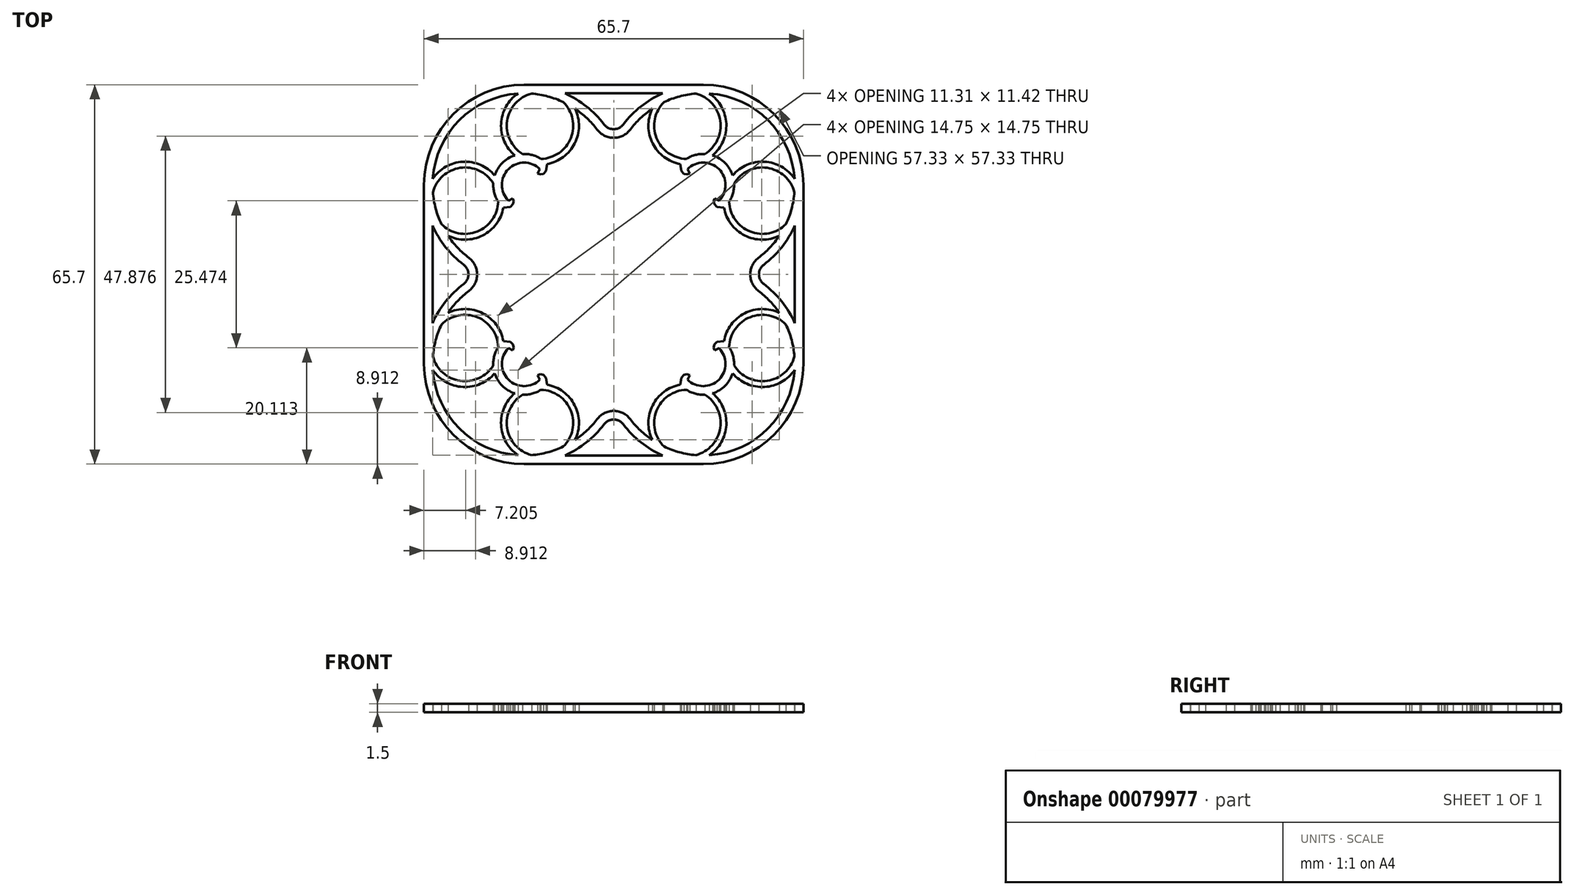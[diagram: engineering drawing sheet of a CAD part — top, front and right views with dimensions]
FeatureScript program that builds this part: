
annotation { "Feature Type Name" : "Feature", "Feature Type Description" : "" }
export const myFeature = defineFeature(function(context is Context, id is Id, definition is map)
    precondition{}
    {
        {
            var Q0;
            Q0=qCreatedBy(makeId("Top.planeOp"),FACE);
            var sketch = newSketch(context, id + "F0", { "sketchPlane" : qUnion([Q0])});
            skLineSegment(sketch, "E0.bottom", {"start": v(-15.5, 15.5) * mm, "end": v(15.5, 15.5) * mm});
            skLineSegment(sketch, "E0.top", {"start": v(-15.5, -15.5) * mm, "end": v(15.5, -15.5) * mm});
            skLineSegment(sketch, "E0.left", {"start": v(-15.5, 15.5) * mm, "end": v(-15.5, -15.5) * mm});
            skLineSegment(sketch, "E0.right", {"start": v(15.5, 15.5) * mm, "end": v(15.5, -15.5) * mm});
            skPoint(sketch, "E0.middle", {"position": v(0, 0) * mm});
            skCircle(sketch, "E1", {"center": v(-15.5, 15.5) * mm, "radius": 15 * mm});
            skCircle(sketch, "E2", {"center": v(15.5, 15.5) * mm, "radius": 15 * mm});
            skCircle(sketch, "E3", {"center": v(-15.5, -15.5) * mm, "radius": 15 * mm});
            skCircle(sketch, "E4", {"center": v(15.5, -15.5) * mm, "radius": 15 * mm});
            skLineSegment(sketch, "E5.bottom", {"start": v(-10, 10) * mm, "end": v(10, 10) * mm});
            skLineSegment(sketch, "E5.top", {"start": v(-10, -10) * mm, "end": v(10, -10) * mm});
            skLineSegment(sketch, "E5.left", {"start": v(-10, 10) * mm, "end": v(-10, -10) * mm});
            skLineSegment(sketch, "E5.right", {"start": v(10, 10) * mm, "end": v(10, -10) * mm});
            skCircle(sketch, "E6", {"center": v(-15.5, 15.5) * mm, "radius": 4.5 * mm});
            skCircle(sketch, "E7", {"center": v(-15.5, 15.5) * mm, "radius": 3.5 * mm});
            skCircle(sketch, "E8", {"center": v(15.5, 15.5) * mm, "radius": 3.5 * mm});
            skCircle(sketch, "E9", {"center": v(15.5, 15.5) * mm, "radius": 4.5 * mm});
            skCircle(sketch, "E10", {"center": v(15.5, -15.5) * mm, "radius": 4.5 * mm});
            skCircle(sketch, "E11", {"center": v(15.5, -15.5) * mm, "radius": 3.5 * mm});
            skCircle(sketch, "E12", {"center": v(-15.5, -15.5) * mm, "radius": 3.5 * mm});
            skCircle(sketch, "E13", {"center": v(-15.5, -15.5) * mm, "radius": 4.5 * mm});
            skLineSegment(sketch, "E14", {"start": v(-15.5, 15.5) * mm, "end": v(-18.68, 12.32) * mm});
            skLineSegment(sketch, "E15", {"start": v(-18.68, 12.32) * mm, "end": v(-12.32, 18.68) * mm});
            skLineSegment(sketch, "E16", {"start": v(-17.9, 11.7) * mm, "end": v(-11.7, 17.9) * mm});
            skLineSegment(sketch, "E17", {"start": v(-13.24, 16.34) * mm, "end": v(-13.95, 17.05) * mm});
            skSolve(sketch);
        }
        {
            var Q0;
            Q0=qCreatedBy(makeId("Top.planeOp"),FACE);
            var sketch = newSketch(context, id + "F1", { "sketchPlane" : qUnion([Q0])});
            skPoint(sketch, "E18.0", {"position": v(-15.5, 15.5) * mm});
            skArc(sketch, "E19", {"start": v(-12.6, 20) * mm, "mid": v(-14.12, 20.67) * mm, "end": v(-15.77, 20.84) * mm});
            skArc(sketch, "E20", {"start": v(-2.86, 25.06) * mm, "mid": v(-4.62, 27.02) * mm, "end": v(-6.67, 28.67) * mm});
            skArc(sketch, "E21", {"start": v(-12.78, 18.22) * mm, "mid": v(-18.22, 18.22) * mm, "end": v(-18.22, 12.78) * mm});
            skLineSegment(sketch, "E22", {"start": v(-15.5, 32.85) * mm, "end": v(0, 32.85) * mm});
            skLineSegment(sketch, "E23", {"start": v(-8.44, 31.35) * mm, "end": v(0, 31.35) * mm});
            skLineSegment(sketch, "E24", {"start": v(-32.85, 15.5) * mm, "end": v(-32.85, 0) * mm});
            skLineSegment(sketch, "E25", {"start": v(-31.35, 8.44) * mm, "end": v(-31.35, 0) * mm});
            skArc(sketch, "E26.trimOffspring", {"start": v(-15.5, 32.85) * mm, "mid": v(-27.77, 27.77) * mm, "end": v(-32.85, 15.5) * mm});
            skPoint(sketch, "E27.orphan", {"position": v(-15.5, 31.35) * mm});
            skArc(sketch, "E28.trimOffspring", {"start": v(-31.35, 8.44) * mm, "mid": v(-29.09, 4.71) * mm, "end": v(-25.97, 1.66) * mm});
            skPoint(sketch, "E29.orphan", {"position": v(-31.35, 15.5) * mm});
            skArc(sketch, "E30", {"start": v(-25.97, -1.66) * mm, "mid": v(-25.14, 0) * mm, "end": v(-25.97, 1.66) * mm});
            skArc(sketch, "E31", {"start": v(-25.06, -2.86) * mm, "mid": v(-23.64, 0) * mm, "end": v(-25.06, 2.86) * mm});
            skLineSegment(sketch, "E32.0", {"start": v(-18.68, 12.32) * mm, "end": v(-18.22, 12.78) * mm});
            skLineSegment(sketch, "E33.0", {"start": v(-17.9, 11.7) * mm, "end": v(-17.42, 12.16) * mm});
            skLineSegment(sketch, "E34", {"start": v(-18.22, 12.78) * mm, "end": v(-17.47, 13.15) * mm});
            skLineSegment(sketch, "E35", {"start": v(-17.47, 13.15) * mm, "end": v(-17.3, 12.68) * mm});
            skLineSegment(sketch, "E36", {"start": v(-17.3, 12.68) * mm, "end": v(-17.42, 12.16) * mm});
            skLineSegment(sketch, "E37", {"start": v(-20.67, 14.12) * mm, "end": v(-30.8, 11.4) * mm});
            skLineSegment(sketch, "E38", {"start": v(-14.12, 20.67) * mm, "end": v(-11.4, 30.8) * mm});
            skArc(sketch, "E39", {"start": v(-20.6, 17.13) * mm, "mid": v(-26.1, 19.5) * mm, "end": v(-31.31, 16.56) * mm});
            skArc(sketch, "E40", {"start": v(-11.54, 19.1) * mm, "mid": v(-6.74, 22.68) * mm, "end": v(-6.67, 28.67) * mm});
            skArc(sketch, "E41", {"start": v(-12.6, 20) * mm, "mid": v(-7.4, 23.62) * mm, "end": v(-8.7, 29.82) * mm});
            skArc(sketch, "E42", {"start": v(-20.84, 15.77) * mm, "mid": v(-26.58, 18.44) * mm, "end": v(-31.3, 14.22) * mm});
            skPoint(sketch, "E43.0", {"position": v(-10, 10) * mm});
            skLineSegment(sketch, "E44.MirrorCS", {"start": v(-12.78, 18.22) * mm, "end": v(-13.15, 17.47) * mm});
            skLineSegment(sketch, "E45.MirrorCS", {"start": v(-12.68, 17.3) * mm, "end": v(-12.16, 17.42) * mm});
            skLineSegment(sketch, "E46.MirrorCS", {"start": v(-13.15, 17.47) * mm, "end": v(-12.68, 17.3) * mm});
            skLineSegment(sketch, "E47", {"start": v(-17.9, 11.7) * mm, "end": v(-19.1, 11.54) * mm});
            skLineSegment(sketch, "E48", {"start": v(-11.7, 17.9) * mm, "end": v(-11.54, 19.1) * mm});
            skArc(sketch, "E49.trimOffspring", {"start": v(-20.84, 15.77) * mm, "mid": v(-20.67, 14.12) * mm, "end": v(-20, 12.6) * mm});
            skArc(sketch, "E50.trimOffspring", {"start": v(-17.13, 20.6) * mm, "mid": v(-19.28, 19.28) * mm, "end": v(-20.6, 17.13) * mm});
            skArc(sketch, "E51.trimOffspring", {"start": v(-8.7, 29.82) * mm, "mid": v(-11.4, 30.8) * mm, "end": v(-14.22, 31.3) * mm});
            skArc(sketch, "E52.trimOffspring", {"start": v(-14.22, 31.3) * mm, "mid": v(-18.44, 26.58) * mm, "end": v(-15.77, 20.84) * mm});
            skArc(sketch, "E53.trimOffspring", {"start": v(-16.56, 31.31) * mm, "mid": v(-19.5, 26.1) * mm, "end": v(-17.13, 20.6) * mm});
            skArc(sketch, "E54.trimOffspring", {"start": v(-16.56, 31.31) * mm, "mid": v(-26.7, 26.7) * mm, "end": v(-31.31, 16.56) * mm});
            skArc(sketch, "E55.trimOffspring", {"start": v(-28.67, 6.67) * mm, "mid": v(-22.68, 6.74) * mm, "end": v(-19.1, 11.54) * mm});
            skArc(sketch, "E56.trimOffspring", {"start": v(-29.82, 8.7) * mm, "mid": v(-23.62, 7.4) * mm, "end": v(-20, 12.6) * mm});
            skArc(sketch, "E57.trimOffspring", {"start": v(-31.3, 14.22) * mm, "mid": v(-30.8, 11.4) * mm, "end": v(-29.82, 8.7) * mm});
            skArc(sketch, "E58.trimOffspring", {"start": v(-28.67, 6.67) * mm, "mid": v(-27.02, 4.62) * mm, "end": v(-25.06, 2.86) * mm});
            skLineSegment(sketch, "E59.trimOffspring", {"start": v(-12.78, 18.22) * mm, "end": v(-12.32, 18.68) * mm});
            skLineSegment(sketch, "E60.trimOffspring", {"start": v(-12.16, 17.42) * mm, "end": v(-11.7, 17.9) * mm});
            skArc(sketch, "E61.1.0", {"start": v(1.66, -25.97) * mm, "mid": v(0, -25.14) * mm, "end": v(-1.66, -25.97) * mm});
            skPoint(sketch, "E61.1.1", {"position": v(-15.5, -31.35) * mm});
            skArc(sketch, "E61.1.2", {"start": v(-18.22, -12.78) * mm, "mid": v(-18.22, -18.22) * mm, "end": v(-12.78, -18.22) * mm});
            skLineSegment(sketch, "E61.1.3", {"start": v(-14.12, -20.67) * mm, "end": v(-11.4, -30.8) * mm});
            skArc(sketch, "E61.1.4", {"start": v(-20, -12.6) * mm, "mid": v(-23.62, -7.4) * mm, "end": v(-29.82, -8.7) * mm});
            skLineSegment(sketch, "E61.1.5", {"start": v(-32.85, -15.5) * mm, "end": v(-32.85, 0) * mm});
            skLineSegment(sketch, "E61.1.6", {"start": v(-8.44, -31.35) * mm, "end": v(0, -31.35) * mm});
            skArc(sketch, "E61.1.7", {"start": v(-20.6, -17.13) * mm, "mid": v(-19.28, -19.28) * mm, "end": v(-17.13, -20.6) * mm});
            skArc(sketch, "E61.1.8", {"start": v(-31.3, -14.22) * mm, "mid": v(-26.58, -18.44) * mm, "end": v(-20.84, -15.77) * mm});
            skArc(sketch, "E61.1.9", {"start": v(-25.06, -2.86) * mm, "mid": v(-27.02, -4.62) * mm, "end": v(-28.67, -6.67) * mm});
            skArc(sketch, "E61.1.11", {"start": v(-31.31, -16.56) * mm, "mid": v(-26.1, -19.5) * mm, "end": v(-20.6, -17.13) * mm});
            skLineSegment(sketch, "E61.1.12", {"start": v(-31.35, -8.44) * mm, "end": v(-31.35, 0) * mm});
            skArc(sketch, "E61.1.13", {"start": v(-32.85, -15.5) * mm, "mid": v(-27.77, -27.77) * mm, "end": v(-15.5, -32.85) * mm});
            skArc(sketch, "E61.1.14", {"start": v(-6.67, -28.67) * mm, "mid": v(-4.62, -27.02) * mm, "end": v(-2.86, -25.06) * mm});
            skLineSegment(sketch, "E61.1.15", {"start": v(-15.5, -32.85) * mm, "end": v(0, -32.85) * mm});
            skArc(sketch, "E61.1.16", {"start": v(-8.44, -31.35) * mm, "mid": v(-4.71, -29.09) * mm, "end": v(-1.66, -25.97) * mm});
            skArc(sketch, "E61.1.17", {"start": v(-8.7, -29.82) * mm, "mid": v(-7.4, -23.62) * mm, "end": v(-12.6, -20) * mm});
            skArc(sketch, "E61.1.18", {"start": v(2.86, -25.06) * mm, "mid": v(0, -23.64) * mm, "end": v(-2.86, -25.06) * mm});
            skPoint(sketch, "E61.1.19", {"position": v(-10, -10) * mm});
            skArc(sketch, "E61.1.20", {"start": v(-19.1, -11.54) * mm, "mid": v(-22.68, -6.74) * mm, "end": v(-28.67, -6.67) * mm});
            skArc(sketch, "E61.1.21", {"start": v(-15.77, -20.84) * mm, "mid": v(-18.44, -26.58) * mm, "end": v(-14.22, -31.3) * mm});
            skArc(sketch, "E61.1.22", {"start": v(-31.31, -16.56) * mm, "mid": v(-26.7, -26.7) * mm, "end": v(-16.56, -31.31) * mm});
            skArc(sketch, "E61.1.23", {"start": v(-6.67, -28.67) * mm, "mid": v(-6.74, -22.68) * mm, "end": v(-11.54, -19.1) * mm});
            skPoint(sketch, "E61.1.24", {"position": v(-15.5, -15.5) * mm});
            skArc(sketch, "E61.1.25", {"start": v(-17.13, -20.6) * mm, "mid": v(-19.5, -26.1) * mm, "end": v(-16.56, -31.31) * mm});
            skLineSegment(sketch, "E61.1.26", {"start": v(-20.67, -14.12) * mm, "end": v(-30.8, -11.4) * mm});
            skPoint(sketch, "E61.1.27", {"position": v(-31.35, -15.5) * mm});
            skArc(sketch, "E61.1.28", {"start": v(-14.22, -31.3) * mm, "mid": v(-11.4, -30.8) * mm, "end": v(-8.7, -29.82) * mm});
            skArc(sketch, "E61.1.29", {"start": v(-20, -12.6) * mm, "mid": v(-20.67, -14.12) * mm, "end": v(-20.84, -15.77) * mm});
            skArc(sketch, "E61.1.30", {"start": v(-15.77, -20.84) * mm, "mid": v(-14.12, -20.67) * mm, "end": v(-12.6, -20) * mm});
            skArc(sketch, "E61.1.31", {"start": v(-29.82, -8.7) * mm, "mid": v(-30.8, -11.4) * mm, "end": v(-31.3, -14.22) * mm});
            skLineSegment(sketch, "E61.1.32", {"start": v(-13.15, -17.47) * mm, "end": v(-12.68, -17.3) * mm});
            skLineSegment(sketch, "E61.1.33", {"start": v(-11.7, -17.9) * mm, "end": v(-11.54, -19.1) * mm});
            skLineSegment(sketch, "E61.1.34", {"start": v(-17.47, -13.15) * mm, "end": v(-17.3, -12.68) * mm});
            skLineSegment(sketch, "E61.1.35", {"start": v(-17.3, -12.68) * mm, "end": v(-17.42, -12.16) * mm});
            skLineSegment(sketch, "E61.1.36", {"start": v(-17.42, -12.16) * mm, "end": v(-17.9, -11.7) * mm});
            skLineSegment(sketch, "E61.1.37", {"start": v(-17.9, -11.7) * mm, "end": v(-19.1, -11.54) * mm});
            skLineSegment(sketch, "E61.1.38", {"start": v(-11.7, -17.9) * mm, "end": v(-12.16, -17.42) * mm});
            skLineSegment(sketch, "E61.1.39", {"start": v(-18.22, -12.78) * mm, "end": v(-18.68, -12.32) * mm});
            skLineSegment(sketch, "E61.1.40", {"start": v(-18.22, -12.78) * mm, "end": v(-17.47, -13.15) * mm});
            skLineSegment(sketch, "E61.1.41", {"start": v(-12.78, -18.22) * mm, "end": v(-13.15, -17.47) * mm});
            skLineSegment(sketch, "E61.1.42", {"start": v(-12.68, -17.3) * mm, "end": v(-12.16, -17.42) * mm});
            skLineSegment(sketch, "E61.1.43", {"start": v(-17.42, -12.16) * mm, "end": v(-17.9, -11.7) * mm});
            skLineSegment(sketch, "E61.1.44", {"start": v(-12.32, -18.68) * mm, "end": v(-12.78, -18.22) * mm});
            skLineSegment(sketch, "E61.1.45", {"start": v(-11.7, -17.9) * mm, "end": v(-12.16, -17.42) * mm});
            skArc(sketch, "E61.2.0", {"start": v(25.97, 1.66) * mm, "mid": v(25.14, 0) * mm, "end": v(25.97, -1.66) * mm});
            skPoint(sketch, "E61.2.1", {"position": v(31.35, -15.5) * mm});
            skArc(sketch, "E61.2.2", {"start": v(12.78, -18.22) * mm, "mid": v(18.22, -18.22) * mm, "end": v(18.22, -12.78) * mm});
            skLineSegment(sketch, "E61.2.3", {"start": v(20.67, -14.12) * mm, "end": v(30.8, -11.4) * mm});
            skArc(sketch, "E61.2.4", {"start": v(12.6, -20) * mm, "mid": v(7.4, -23.62) * mm, "end": v(8.7, -29.82) * mm});
            skLineSegment(sketch, "E61.2.5", {"start": v(15.5, -32.85) * mm, "end": v(0, -32.85) * mm});
            skLineSegment(sketch, "E61.2.6", {"start": v(31.35, -8.44) * mm, "end": v(31.35, 0) * mm});
            skArc(sketch, "E61.2.7", {"start": v(17.13, -20.6) * mm, "mid": v(19.28, -19.28) * mm, "end": v(20.6, -17.13) * mm});
            skArc(sketch, "E61.2.8", {"start": v(14.22, -31.3) * mm, "mid": v(18.44, -26.58) * mm, "end": v(15.77, -20.84) * mm});
            skArc(sketch, "E61.2.9", {"start": v(2.86, -25.06) * mm, "mid": v(4.62, -27.02) * mm, "end": v(6.67, -28.67) * mm});
            skArc(sketch, "E61.2.11", {"start": v(16.56, -31.31) * mm, "mid": v(19.5, -26.1) * mm, "end": v(17.13, -20.6) * mm});
            skLineSegment(sketch, "E61.2.12", {"start": v(8.44, -31.35) * mm, "end": v(0, -31.35) * mm});
            skArc(sketch, "E61.2.13", {"start": v(15.5, -32.85) * mm, "mid": v(27.77, -27.77) * mm, "end": v(32.85, -15.5) * mm});
            skArc(sketch, "E61.2.14", {"start": v(28.67, -6.67) * mm, "mid": v(27.02, -4.62) * mm, "end": v(25.06, -2.86) * mm});
            skLineSegment(sketch, "E61.2.15", {"start": v(32.85, -15.5) * mm, "end": v(32.85, 0) * mm});
            skArc(sketch, "E61.2.16", {"start": v(31.35, -8.44) * mm, "mid": v(29.09, -4.71) * mm, "end": v(25.97, -1.66) * mm});
            skArc(sketch, "E61.2.17", {"start": v(29.82, -8.7) * mm, "mid": v(23.62, -7.4) * mm, "end": v(20, -12.6) * mm});
            skArc(sketch, "E61.2.18", {"start": v(25.06, 2.86) * mm, "mid": v(23.64, 0) * mm, "end": v(25.06, -2.86) * mm});
            skPoint(sketch, "E61.2.19", {"position": v(10, -10) * mm});
            skArc(sketch, "E61.2.20", {"start": v(11.54, -19.1) * mm, "mid": v(6.74, -22.68) * mm, "end": v(6.67, -28.67) * mm});
            skArc(sketch, "E61.2.21", {"start": v(20.84, -15.77) * mm, "mid": v(26.58, -18.44) * mm, "end": v(31.3, -14.22) * mm});
            skArc(sketch, "E61.2.22", {"start": v(16.56, -31.31) * mm, "mid": v(26.7, -26.7) * mm, "end": v(31.31, -16.56) * mm});
            skArc(sketch, "E61.2.23", {"start": v(28.67, -6.67) * mm, "mid": v(22.68, -6.74) * mm, "end": v(19.1, -11.54) * mm});
            skPoint(sketch, "E61.2.24", {"position": v(15.5, -15.5) * mm});
            skArc(sketch, "E61.2.25", {"start": v(20.6, -17.13) * mm, "mid": v(26.1, -19.5) * mm, "end": v(31.31, -16.56) * mm});
            skLineSegment(sketch, "E61.2.26", {"start": v(14.12, -20.67) * mm, "end": v(11.4, -30.8) * mm});
            skPoint(sketch, "E61.2.27", {"position": v(15.5, -31.35) * mm});
            skArc(sketch, "E61.2.28", {"start": v(31.3, -14.22) * mm, "mid": v(30.8, -11.4) * mm, "end": v(29.82, -8.7) * mm});
            skArc(sketch, "E61.2.29", {"start": v(12.6, -20) * mm, "mid": v(14.12, -20.67) * mm, "end": v(15.77, -20.84) * mm});
            skArc(sketch, "E61.2.30", {"start": v(20.84, -15.77) * mm, "mid": v(20.67, -14.12) * mm, "end": v(20, -12.6) * mm});
            skArc(sketch, "E61.2.31", {"start": v(8.7, -29.82) * mm, "mid": v(11.4, -30.8) * mm, "end": v(14.22, -31.3) * mm});
            skLineSegment(sketch, "E61.2.32", {"start": v(17.47, -13.15) * mm, "end": v(17.3, -12.68) * mm});
            skLineSegment(sketch, "E61.2.33", {"start": v(17.9, -11.7) * mm, "end": v(19.1, -11.54) * mm});
            skLineSegment(sketch, "E61.2.34", {"start": v(13.15, -17.47) * mm, "end": v(12.68, -17.3) * mm});
            skLineSegment(sketch, "E61.2.35", {"start": v(12.68, -17.3) * mm, "end": v(12.16, -17.42) * mm});
            skLineSegment(sketch, "E61.2.36", {"start": v(12.16, -17.42) * mm, "end": v(11.7, -17.9) * mm});
            skLineSegment(sketch, "E61.2.37", {"start": v(11.7, -17.9) * mm, "end": v(11.54, -19.1) * mm});
            skLineSegment(sketch, "E61.2.38", {"start": v(17.9, -11.7) * mm, "end": v(17.42, -12.16) * mm});
            skLineSegment(sketch, "E61.2.39", {"start": v(12.78, -18.22) * mm, "end": v(12.32, -18.68) * mm});
            skLineSegment(sketch, "E61.2.40", {"start": v(12.78, -18.22) * mm, "end": v(13.15, -17.47) * mm});
            skLineSegment(sketch, "E61.2.41", {"start": v(18.22, -12.78) * mm, "end": v(17.47, -13.15) * mm});
            skLineSegment(sketch, "E61.2.42", {"start": v(17.3, -12.68) * mm, "end": v(17.42, -12.16) * mm});
            skLineSegment(sketch, "E61.2.43", {"start": v(12.16, -17.42) * mm, "end": v(11.7, -17.9) * mm});
            skLineSegment(sketch, "E61.2.44", {"start": v(18.68, -12.32) * mm, "end": v(18.22, -12.78) * mm});
            skLineSegment(sketch, "E61.2.45", {"start": v(17.9, -11.7) * mm, "end": v(17.42, -12.16) * mm});
            skArc(sketch, "E61.3.0", {"start": v(-1.66, 25.97) * mm, "mid": v(0, 25.14) * mm, "end": v(1.66, 25.97) * mm});
            skPoint(sketch, "E61.3.1", {"position": v(15.5, 31.35) * mm});
            skArc(sketch, "E61.3.2", {"start": v(18.22, 12.78) * mm, "mid": v(18.22, 18.22) * mm, "end": v(12.78, 18.22) * mm});
            skLineSegment(sketch, "E61.3.3", {"start": v(14.12, 20.67) * mm, "end": v(11.4, 30.8) * mm});
            skArc(sketch, "E61.3.4", {"start": v(20, 12.6) * mm, "mid": v(23.62, 7.4) * mm, "end": v(29.82, 8.7) * mm});
            skLineSegment(sketch, "E61.3.5", {"start": v(32.85, 15.5) * mm, "end": v(32.85, 0) * mm});
            skLineSegment(sketch, "E61.3.6", {"start": v(8.44, 31.35) * mm, "end": v(0, 31.35) * mm});
            skArc(sketch, "E61.3.7", {"start": v(20.6, 17.13) * mm, "mid": v(19.28, 19.28) * mm, "end": v(17.13, 20.6) * mm});
            skArc(sketch, "E61.3.8", {"start": v(31.3, 14.22) * mm, "mid": v(26.58, 18.44) * mm, "end": v(20.84, 15.77) * mm});
            skArc(sketch, "E61.3.9", {"start": v(25.06, 2.86) * mm, "mid": v(27.02, 4.62) * mm, "end": v(28.67, 6.67) * mm});
            skArc(sketch, "E61.3.10", {"start": v(25.97, 1.66) * mm, "mid": v(29.09, 4.71) * mm, "end": v(31.35, 8.44) * mm});
            skArc(sketch, "E61.3.11", {"start": v(31.31, 16.56) * mm, "mid": v(26.1, 19.5) * mm, "end": v(20.6, 17.13) * mm});
            skLineSegment(sketch, "E61.3.12", {"start": v(31.35, 8.44) * mm, "end": v(31.35, 0) * mm});
            skArc(sketch, "E61.3.13", {"start": v(32.85, 15.5) * mm, "mid": v(27.77, 27.77) * mm, "end": v(15.5, 32.85) * mm});
            skArc(sketch, "E61.3.14", {"start": v(6.67, 28.67) * mm, "mid": v(4.62, 27.02) * mm, "end": v(2.86, 25.06) * mm});
            skLineSegment(sketch, "E61.3.15", {"start": v(15.5, 32.85) * mm, "end": v(0, 32.85) * mm});
            skArc(sketch, "E61.3.16", {"start": v(8.44, 31.35) * mm, "mid": v(4.71, 29.09) * mm, "end": v(1.66, 25.97) * mm});
            skArc(sketch, "E61.3.17", {"start": v(8.7, 29.82) * mm, "mid": v(7.4, 23.62) * mm, "end": v(12.6, 20) * mm});
            skArc(sketch, "E61.3.18", {"start": v(-2.86, 25.06) * mm, "mid": v(0, 23.64) * mm, "end": v(2.86, 25.06) * mm});
            skPoint(sketch, "E61.3.19", {"position": v(10, 10) * mm});
            skArc(sketch, "E61.3.20", {"start": v(19.1, 11.54) * mm, "mid": v(22.68, 6.74) * mm, "end": v(28.67, 6.67) * mm});
            skArc(sketch, "E61.3.21", {"start": v(15.77, 20.84) * mm, "mid": v(18.44, 26.58) * mm, "end": v(14.22, 31.3) * mm});
            skArc(sketch, "E61.3.22", {"start": v(31.31, 16.56) * mm, "mid": v(26.7, 26.7) * mm, "end": v(16.56, 31.31) * mm});
            skArc(sketch, "E61.3.23", {"start": v(6.67, 28.67) * mm, "mid": v(6.74, 22.68) * mm, "end": v(11.54, 19.1) * mm});
            skPoint(sketch, "E61.3.24", {"position": v(15.5, 15.5) * mm});
            skArc(sketch, "E61.3.25", {"start": v(17.13, 20.6) * mm, "mid": v(19.5, 26.1) * mm, "end": v(16.56, 31.31) * mm});
            skLineSegment(sketch, "E61.3.26", {"start": v(20.67, 14.12) * mm, "end": v(30.8, 11.4) * mm});
            skPoint(sketch, "E61.3.27", {"position": v(31.35, 15.5) * mm});
            skArc(sketch, "E61.3.28", {"start": v(14.22, 31.3) * mm, "mid": v(11.4, 30.8) * mm, "end": v(8.7, 29.82) * mm});
            skArc(sketch, "E61.3.29", {"start": v(20, 12.6) * mm, "mid": v(20.67, 14.12) * mm, "end": v(20.84, 15.77) * mm});
            skArc(sketch, "E61.3.30", {"start": v(15.77, 20.84) * mm, "mid": v(14.12, 20.67) * mm, "end": v(12.6, 20) * mm});
            skArc(sketch, "E61.3.31", {"start": v(29.82, 8.7) * mm, "mid": v(30.8, 11.4) * mm, "end": v(31.3, 14.22) * mm});
            skLineSegment(sketch, "E61.3.32", {"start": v(13.15, 17.47) * mm, "end": v(12.68, 17.3) * mm});
            skLineSegment(sketch, "E61.3.33", {"start": v(11.7, 17.9) * mm, "end": v(11.54, 19.1) * mm});
            skLineSegment(sketch, "E61.3.34", {"start": v(17.47, 13.15) * mm, "end": v(17.3, 12.68) * mm});
            skLineSegment(sketch, "E61.3.35", {"start": v(17.3, 12.68) * mm, "end": v(17.42, 12.16) * mm});
            skLineSegment(sketch, "E61.3.36", {"start": v(17.42, 12.16) * mm, "end": v(17.9, 11.7) * mm});
            skLineSegment(sketch, "E61.3.37", {"start": v(17.9, 11.7) * mm, "end": v(19.1, 11.54) * mm});
            skLineSegment(sketch, "E61.3.38", {"start": v(11.7, 17.9) * mm, "end": v(12.16, 17.42) * mm});
            skLineSegment(sketch, "E61.3.39", {"start": v(18.22, 12.78) * mm, "end": v(18.68, 12.32) * mm});
            skLineSegment(sketch, "E61.3.40", {"start": v(18.22, 12.78) * mm, "end": v(17.47, 13.15) * mm});
            skLineSegment(sketch, "E61.3.41", {"start": v(12.78, 18.22) * mm, "end": v(13.15, 17.47) * mm});
            skLineSegment(sketch, "E61.3.42", {"start": v(12.68, 17.3) * mm, "end": v(12.16, 17.42) * mm});
            skLineSegment(sketch, "E61.3.43", {"start": v(17.42, 12.16) * mm, "end": v(17.9, 11.7) * mm});
            skLineSegment(sketch, "E61.3.44", {"start": v(12.32, 18.68) * mm, "end": v(12.78, 18.22) * mm});
            skLineSegment(sketch, "E61.3.45", {"start": v(11.7, 17.9) * mm, "end": v(12.16, 17.42) * mm});
            skPoint(sketch, "E61.center", {"position": v(0, 0) * mm});
            skArc(sketch, "E62.trimOffspring", {"start": v(-1.66, 25.97) * mm, "mid": v(-4.71, 29.09) * mm, "end": v(-8.44, 31.35) * mm});
            skPoint(sketch, "E63.orphan", {"position": v(0, 18.81) * mm});
            skPoint(sketch, "E64.orphan", {"position": v(-3.59, 27.23) * mm});
            skPoint(sketch, "E65.orphan", {"position": v(-2.09, 27.23) * mm});
            skPoint(sketch, "E66.orphan", {"position": v(23.3, 0) * mm});
            skPoint(sketch, "E67.orphan", {"position": v(18.81, 0) * mm});
            skPoint(sketch, "E68.orphan", {"position": v(27.23, 3.59) * mm});
            skPoint(sketch, "E69.orphan", {"position": v(27.23, 2.09) * mm});
            skPoint(sketch, "E70.orphan", {"position": v(3.59, -27.23) * mm});
            skPoint(sketch, "E71.orphan", {"position": v(2.09, -27.23) * mm});
            skArc(sketch, "E72.trimOffspring", {"start": v(1.66, -25.97) * mm, "mid": v(4.71, -29.09) * mm, "end": v(8.44, -31.35) * mm});
            skPoint(sketch, "E73.orphan", {"position": v(0, -18.81) * mm});
            skPoint(sketch, "E74.orphan", {"position": v(-27.23, -2.09) * mm});
            skArc(sketch, "E75.trimOffspring", {"start": v(-25.97, -1.66) * mm, "mid": v(-29.09, -4.71) * mm, "end": v(-31.35, -8.44) * mm});
            skPoint(sketch, "E76.orphan", {"position": v(-18.81, 0) * mm});
            skPoint(sketch, "E77.orphan", {"position": v(-27.23, -3.59) * mm});
            skSolve(sketch);
        }
        {
            var Q0;
            Q0 = qSketchRegion(id + "F1", true);
            extrude(context, id + "F2", {"entities" : qUnion([Q0]), "depth" : 1.5 * mm});
        }
    });
